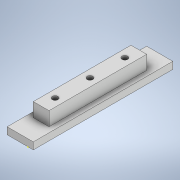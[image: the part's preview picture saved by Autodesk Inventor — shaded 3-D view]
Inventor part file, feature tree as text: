
AUTODESK INVENTOR PART (.ipt)
format: ipt  version: 2022 (Build 260153000, 153)  size: 124,928 bytes
history: native  units: in
note: dims shown in document units (in); Inventor stores cm internally (conversion verified against a paired STEP export)
features: sketch x3, extrude x2
ambient origin geometry x8: Origin, YZ Plane, XZ Plane, XY Plane, X Axis, Y Axis, Z Axis, Center Point
bodies: Solid1 (feature_tree)
feature tree (5):
  extrude  "Extrusion1"  Depth=3.1496in
  extrude  "Extrusion2"  Depth=0.1575in
  sketch  "Sketch3"  dims[d5=0.7874in d6=0.7874in d7=0.1299in d8=0.1299in d9=0.1299in d10=0.4724in d11=0.4724in d12=0.3543in d13=0.315in d14=0.0in]
  sketch  "Sketch1"  dims[d0=0.5906in d1=3.1496in]
  sketch  "Sketch2"  dims[d2=0.1575in d3=0.0in d4=0.7874in]
